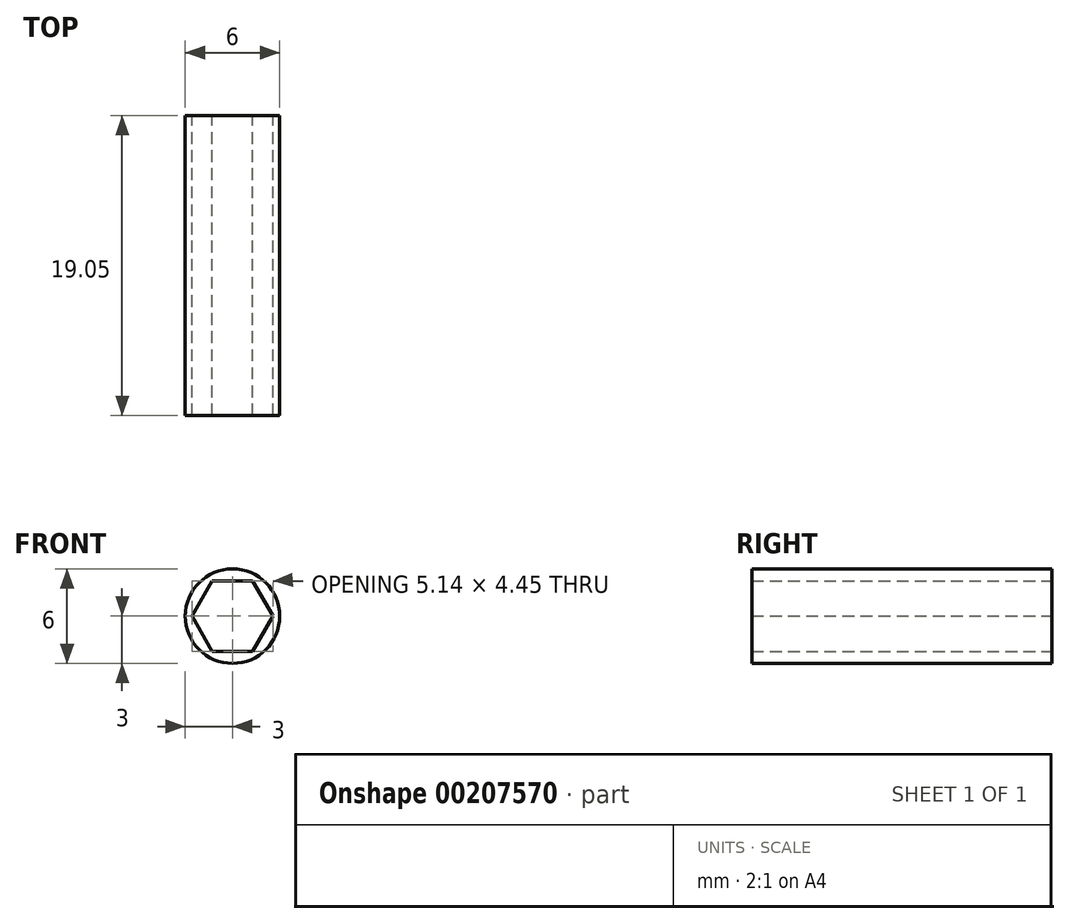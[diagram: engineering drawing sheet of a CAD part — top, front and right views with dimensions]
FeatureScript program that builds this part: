
annotation { "Feature Type Name" : "Feature", "Feature Type Description" : "" }
export const myFeature = defineFeature(function(context is Context, id is Id, definition is map)
    precondition{}
    {
        {
            var Q0;
            Q0=qCreatedBy(makeId("Front.planeOp"),FACE);
            var sketch = newSketch(context, id + "F0", { "sketchPlane" : qUnion([Q0])});
            skCircle(sketch, "E0.cCircle", {"center": v(0, 0) * mm, "radius": 2.23 * mm, "construction": true});
            skLineSegment(sketch, "E0.0", {"start": v(2.57, 0) * mm, "end": v(1.28, -2.22) * mm});
            skLineSegment(sketch, "E0.1", {"start": v(1.28, -2.23) * mm, "end": v(-1.28, -2.23) * mm});
            skLineSegment(sketch, "E0.2", {"start": v(-1.28, -2.22) * mm, "end": v(-2.57, 0) * mm});
            skLineSegment(sketch, "E0.3", {"start": v(-2.57, 0) * mm, "end": v(-1.28, 2.23) * mm});
            skLineSegment(sketch, "E0.4", {"start": v(-1.28, 2.23) * mm, "end": v(1.28, 2.23) * mm});
            skLineSegment(sketch, "E0.5", {"start": v(1.28, 2.23) * mm, "end": v(2.57, 0) * mm});
            skPoint(sketch, "E0.0.midPoint", {"position": v(1.93, -1.11) * mm});
            skLineSegment(sketch, "E1", {"start": v(0, 2.23) * mm, "end": v(0, -2.23) * mm, "construction": true});
            skCircle(sketch, "E2", {"center": v(0, 0) * mm, "radius": 3 * mm});
            skLineSegment(sketch, "E3", {"start": v(-2.57, 0) * mm, "end": v(2.57, 0) * mm, "construction": true});
            skSolve(sketch);
        }
        {
            var Q0;
            Q0=makeQuery(id+"F0.imprint","IMPRINT",FACE,{"disambiguationData":[TD([[makeQuery(id+"F0.imprint","IMPRINT",EDGE,{"derivedFrom":sQuery(id+"F0.wireOp",EDGE,"E0.0")}),1.0]])]});
            extrude(context, id + "F1", {"entities" : qUnion([Q0]), "depth" : 19.05 * mm});
        }
    });
